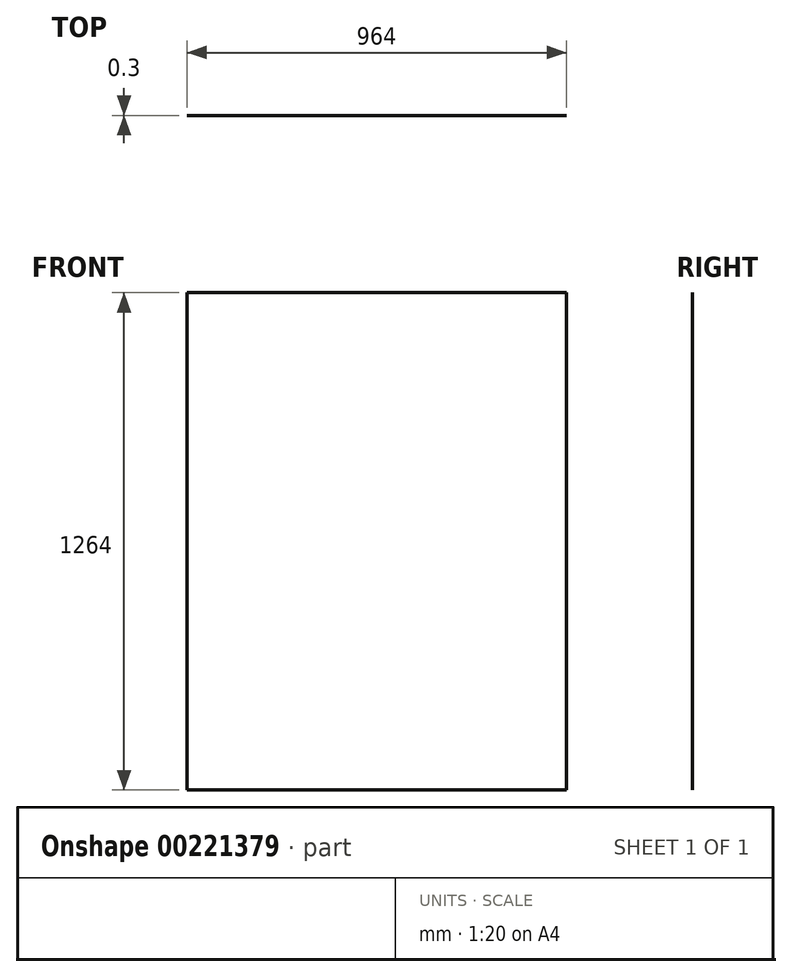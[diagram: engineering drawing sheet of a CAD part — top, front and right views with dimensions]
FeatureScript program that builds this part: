
annotation { "Feature Type Name" : "Feature", "Feature Type Description" : "" }
export const myFeature = defineFeature(function(context is Context, id is Id, definition is map)
    precondition{}
    {
        {
            var Q0;
            Q0=qCreatedBy(makeId("Front.planeOp"),FACE);
            var sketch = newSketch(context, id + "F0", { "sketchPlane" : qUnion([Q0])});
            skLineSegment(sketch, "E0.bottom", {"start": v(482, -632) * mm, "end": v(-482, -632) * mm});
            skLineSegment(sketch, "E0.top", {"start": v(482, 632) * mm, "end": v(-482, 632) * mm});
            skLineSegment(sketch, "E0.left", {"start": v(482, -632) * mm, "end": v(482, 632) * mm});
            skLineSegment(sketch, "E0.right", {"start": v(-482, -632) * mm, "end": v(-482, 632) * mm});
            skPoint(sketch, "E0.middle", {"position": v(0, 0) * mm});
            skSolve(sketch);
        }
        {
            var Q0;
            Q0=qSketchRegion(id+"F0",true);
            extrude(context, id + "F1", {"entities" : qUnion([Q0]), "depth" : 0.3 * mm});
        }
    });
